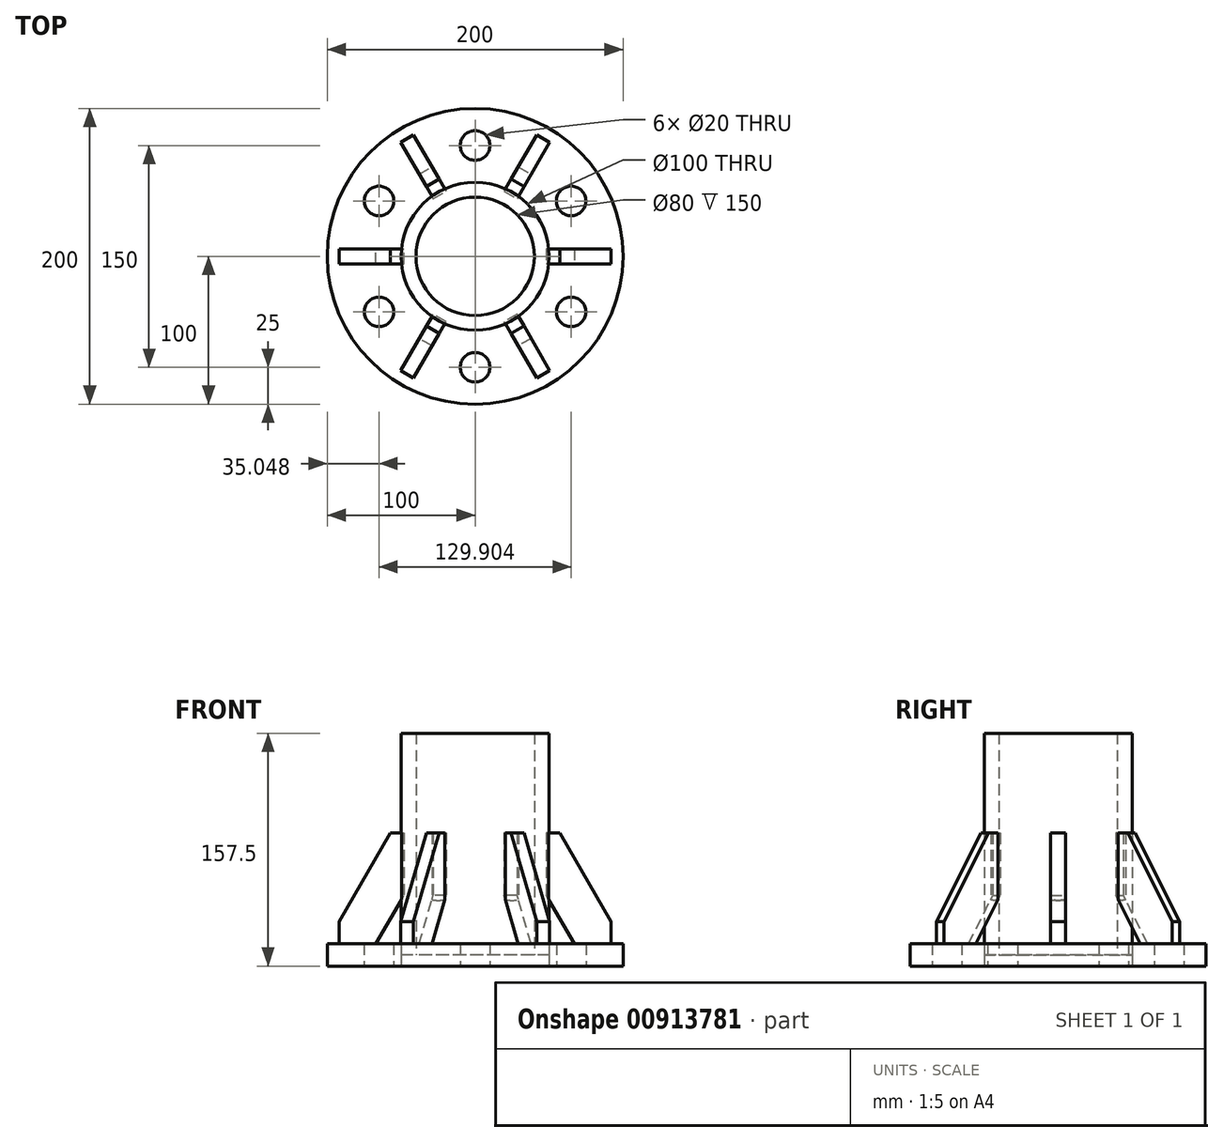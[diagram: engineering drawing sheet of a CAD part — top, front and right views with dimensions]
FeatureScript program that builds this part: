
annotation { "Feature Type Name" : "Feature", "Feature Type Description" : "" }
export const myFeature = defineFeature(function(context is Context, id is Id, definition is map)
    precondition{}
    {
        {
            var Q0;
            Q0=qCreatedBy(makeId("Top.planeOp"),FACE);
            var sketch = newSketch(context, id + "F0", { "sketchPlane" : qUnion([Q0])});
            skCircle(sketch, "E0", {"center": v(0, 0) * mm, "radius": 100 * mm});
            skCircle(sketch, "E1", {"center": v(0, 0) * mm, "radius": 50 * mm});
            skCircle(sketch, "E2", {"center": v(0, 0) * mm, "radius": 40 * mm});
            skCircle(sketch, "E3", {"center": v(0, 0) * mm, "radius": 75 * mm, "construction": true});
            skCircle(sketch, "E4", {"center": v(0, 75) * mm, "radius": 10 * mm});
            skCircle(sketch, "E5.1.0", {"center": v(-64.95, 37.5) * mm, "radius": 10 * mm});
            skCircle(sketch, "E5.2.0", {"center": v(-64.95, -37.5) * mm, "radius": 10 * mm});
            skCircle(sketch, "E5.3.0", {"center": v(0, -75) * mm, "radius": 10 * mm});
            skCircle(sketch, "E5.4.0", {"center": v(64.95, -37.5) * mm, "radius": 10 * mm});
            skCircle(sketch, "E5.5.0", {"center": v(64.95, 37.5) * mm, "radius": 10 * mm});
            skSolve(sketch);
        }
        {
            var Q0;
            Q0=makeQuery(id+"F0.imprint","IMPRINT",FACE,{"disambiguationData":[TD([[makeQuery(id+"F0.imprint","IMPRINT",EDGE,{"derivedFrom":sQuery(id+"F0.wireOp",EDGE,"E1")}),1.0]])]});
            extrude(context, id + "F1", {"entities" : qUnion([Q0]), "depth" : 157.5 * mm, "offsetDistance" : 25 * mm});
        }
        {
            var Q0;
            Q0=makeQuery(id+"F0.imprint","IMPRINT",FACE,{"disambiguationData":[TD([[makeQuery(id+"F0.imprint","IMPRINT",EDGE,{"derivedFrom":sQuery(id+"F0.wireOp",EDGE,"E0")}),1.0]])]});
            extrude(context, id + "F2", {"entities" : qUnion([Q0]), "depth" : 15 * mm, "offsetDistance" : 25 * mm});
        }
        {
            var Q0;
            Q0=makeQuery(id+"F0.imprint","IMPRINT",FACE,{"disambiguationData":[TD([[makeQuery(id+"F0.imprint","IMPRINT",EDGE,{"derivedFrom":sQuery(id+"F0.wireOp",EDGE,"E2")}),1.0]])]});
            var Q1;
            Q1=makeQuery(id+"F0.imprint","IMPRINT",FACE,{"disambiguationData":[TD([[makeQuery(id+"F0.imprint","IMPRINT",EDGE,{"derivedFrom":sQuery(id+"F0.wireOp",EDGE,"E1")}),1.0]])]});
            extrude(context, id + "F3", {"entities" : qUnion([Q0, Q1]), "depth" : 7.5 * mm, "offsetDistance" : 25 * mm});
        }
        {
            var Q0;
            Q0=qCreatedBy(makeId("Front.planeOp"),FACE);
            var sketch = newSketch(context, id + "F4", { "sketchPlane" : qUnion([Q0])});
            skLineSegment(sketch, "E6.0", {"start": v(-100, 15) * mm, "end": v(-50, 15) * mm});
            skLineSegment(sketch, "E7", {"start": v(-100, 15) * mm, "end": v(-92, 15) * mm, "construction": true});
            skLineSegment(sketch, "E8", {"start": v(-92, 15) * mm, "end": v(-67, 15) * mm, "construction": true});
            skLineSegment(sketch, "E9", {"start": v(-92, 15) * mm, "end": v(-92, 30) * mm});
            skLineSegment(sketch, "E10", {"start": v(-67, 15) * mm, "end": v(-48, 47.9) * mm});
            skLineSegment(sketch, "E11", {"start": v(0, 0) * mm, "end": v(-48, 0) * mm, "construction": true});
            skLineSegment(sketch, "E12", {"start": v(-92, 30) * mm, "end": v(-57.36, 90) * mm});
            skLineSegment(sketch, "E13", {"start": v(-57.36, 90) * mm, "end": v(-48, 90) * mm});
            skPoint(sketch, "E14.orphan", {"position": v(-50, 102.75) * mm});
            skPoint(sketch, "E15.orphan", {"position": v(100, 15) * mm});
            skLineSegment(sketch, "E16", {"start": v(-48, 90) * mm, "end": v(-48, 47.9) * mm});
            skLineSegment(sketch, "E17", {"start": v(-48, 0) * mm, "end": v(-48, 110.57) * mm, "construction": true});
            skLineSegment(sketch, "E18", {"start": v(0, 1.7) * mm, "end": v(0, 80.97) * mm, "construction": true});
            skSolve(sketch);
        }
        {
            var Q0;
            {var subQ1=sQuery(id+"F4.wireOp",EDGE,"E9");Q0=makeQuery(id+"F4.imprint","IMPRINT",FACE,{"disambiguationData":[TD([[makeQuery(id+"F4.imprint","IMPRINT",EDGE,{"derivedFrom":subQ1}),-1.0]])]});}
            extrude(context, id + "F5", {"entities" : qUnion([Q0]), "depth" : 10 * mm, "offsetDistance" : 25 * mm, "symmetric" : true});
        }
        {
            var Q0;
            Q0=makeQuery(id+"F5.opExtrude","SWEPT_BODY",BODY,{"disambiguationData":[OSD([sQuery(id+"F4.wireOp",EDGE,"E6.0"),sQuery(id+"F4.wireOp",EDGE,"E9"),sQuery(id+"F4.wireOp",EDGE,"E10"),sQuery(id+"F4.wireOp",EDGE,"E12"),sQuery(id+"F4.wireOp",EDGE,"E13"),sQuery(id+"F4.wireOp",EDGE,"E16")])]});
            var Q1;
            Q1=sQuery(id+"F4.wireOp",EDGE,"E18");
            circularPattern(context, id + "F6", {"entities" : qUnion([Q0]), "axis" : qUnion([Q1]), "angle" : 360 * degree, "instanceCount" : 6, "equalSpace" : true});
        }
        {
            var Q0;
            Q0=makeQuery(id+"F3.opExtrude","SWEPT_BODY",BODY,{"disambiguationData":[OSD([sQuery(id+"F0.wireOp",EDGE,"E1")])]});
            var Q1;
            Q1=makeQuery(id+"F1.opExtrude","SWEPT_BODY",BODY,{"disambiguationData":[OSD([sQuery(id+"F0.wireOp",EDGE,"E1"),sQuery(id+"F0.wireOp",EDGE,"E2")])]});
            booleanBodies(context, id + "F7", {"operationType" : BooleanOperationType.SUBTRACTION, "tools" : qUnion([Q0]), "targets" : qUnion([Q1]), "keepTools" : true});
        }
        {
            var Q0;
            Q0=makeQuery(id+"F6.opPattern","COPY",BODY,{"derivedFrom":makeQuery(id+"F5.opExtrude","SWEPT_BODY",BODY,{"disambiguationData":[OSD([sQuery(id+"F4.wireOp",EDGE,"E6.0"),sQuery(id+"F4.wireOp",EDGE,"E9"),sQuery(id+"F4.wireOp",EDGE,"E10"),sQuery(id+"F4.wireOp",EDGE,"E12"),sQuery(id+"F4.wireOp",EDGE,"E13"),sQuery(id+"F4.wireOp",EDGE,"E16")])]}),"instanceName":"4"});
            var Q1;
            Q1=makeQuery(id+"F6.opPattern","COPY",BODY,{"derivedFrom":makeQuery(id+"F5.opExtrude","SWEPT_BODY",BODY,{"disambiguationData":[OSD([sQuery(id+"F4.wireOp",EDGE,"E6.0"),sQuery(id+"F4.wireOp",EDGE,"E9"),sQuery(id+"F4.wireOp",EDGE,"E10"),sQuery(id+"F4.wireOp",EDGE,"E12"),sQuery(id+"F4.wireOp",EDGE,"E13"),sQuery(id+"F4.wireOp",EDGE,"E16")])]}),"instanceName":"3"});
            var Q2;
            Q2=makeQuery(id+"F6.opPattern","COPY",BODY,{"derivedFrom":makeQuery(id+"F5.opExtrude","SWEPT_BODY",BODY,{"disambiguationData":[OSD([sQuery(id+"F4.wireOp",EDGE,"E6.0"),sQuery(id+"F4.wireOp",EDGE,"E9"),sQuery(id+"F4.wireOp",EDGE,"E10"),sQuery(id+"F4.wireOp",EDGE,"E12"),sQuery(id+"F4.wireOp",EDGE,"E13"),sQuery(id+"F4.wireOp",EDGE,"E16")])]}),"instanceName":"5"});
            var Q3;
            Q3=makeQuery(id+"F5.opExtrude","SWEPT_BODY",BODY,{"disambiguationData":[OSD([sQuery(id+"F4.wireOp",EDGE,"E6.0"),sQuery(id+"F4.wireOp",EDGE,"E9"),sQuery(id+"F4.wireOp",EDGE,"E10"),sQuery(id+"F4.wireOp",EDGE,"E12"),sQuery(id+"F4.wireOp",EDGE,"E13"),sQuery(id+"F4.wireOp",EDGE,"E16")])]});
            var Q4;
            Q4=makeQuery(id+"F6.opPattern","COPY",BODY,{"derivedFrom":makeQuery(id+"F5.opExtrude","SWEPT_BODY",BODY,{"disambiguationData":[OSD([sQuery(id+"F4.wireOp",EDGE,"E6.0"),sQuery(id+"F4.wireOp",EDGE,"E9"),sQuery(id+"F4.wireOp",EDGE,"E10"),sQuery(id+"F4.wireOp",EDGE,"E12"),sQuery(id+"F4.wireOp",EDGE,"E13"),sQuery(id+"F4.wireOp",EDGE,"E16")])]}),"instanceName":"1"});
            var Q5;
            Q5=makeQuery(id+"F6.opPattern","COPY",BODY,{"derivedFrom":makeQuery(id+"F5.opExtrude","SWEPT_BODY",BODY,{"disambiguationData":[OSD([sQuery(id+"F4.wireOp",EDGE,"E6.0"),sQuery(id+"F4.wireOp",EDGE,"E9"),sQuery(id+"F4.wireOp",EDGE,"E10"),sQuery(id+"F4.wireOp",EDGE,"E12"),sQuery(id+"F4.wireOp",EDGE,"E13"),sQuery(id+"F4.wireOp",EDGE,"E16")])]}),"instanceName":"2"});
            var Q6;
            Q6=makeQuery(id+"F1.opExtrude","SWEPT_BODY",BODY,{"disambiguationData":[OSD([sQuery(id+"F0.wireOp",EDGE,"E1"),sQuery(id+"F0.wireOp",EDGE,"E2")])]});
            booleanBodies(context, id + "F8", {"operationType" : BooleanOperationType.SUBTRACTION, "tools" : qUnion([Q0, Q1, Q2, Q3, Q4, Q5]), "targets" : qUnion([Q6]), "keepTools" : true});
        }
    });
